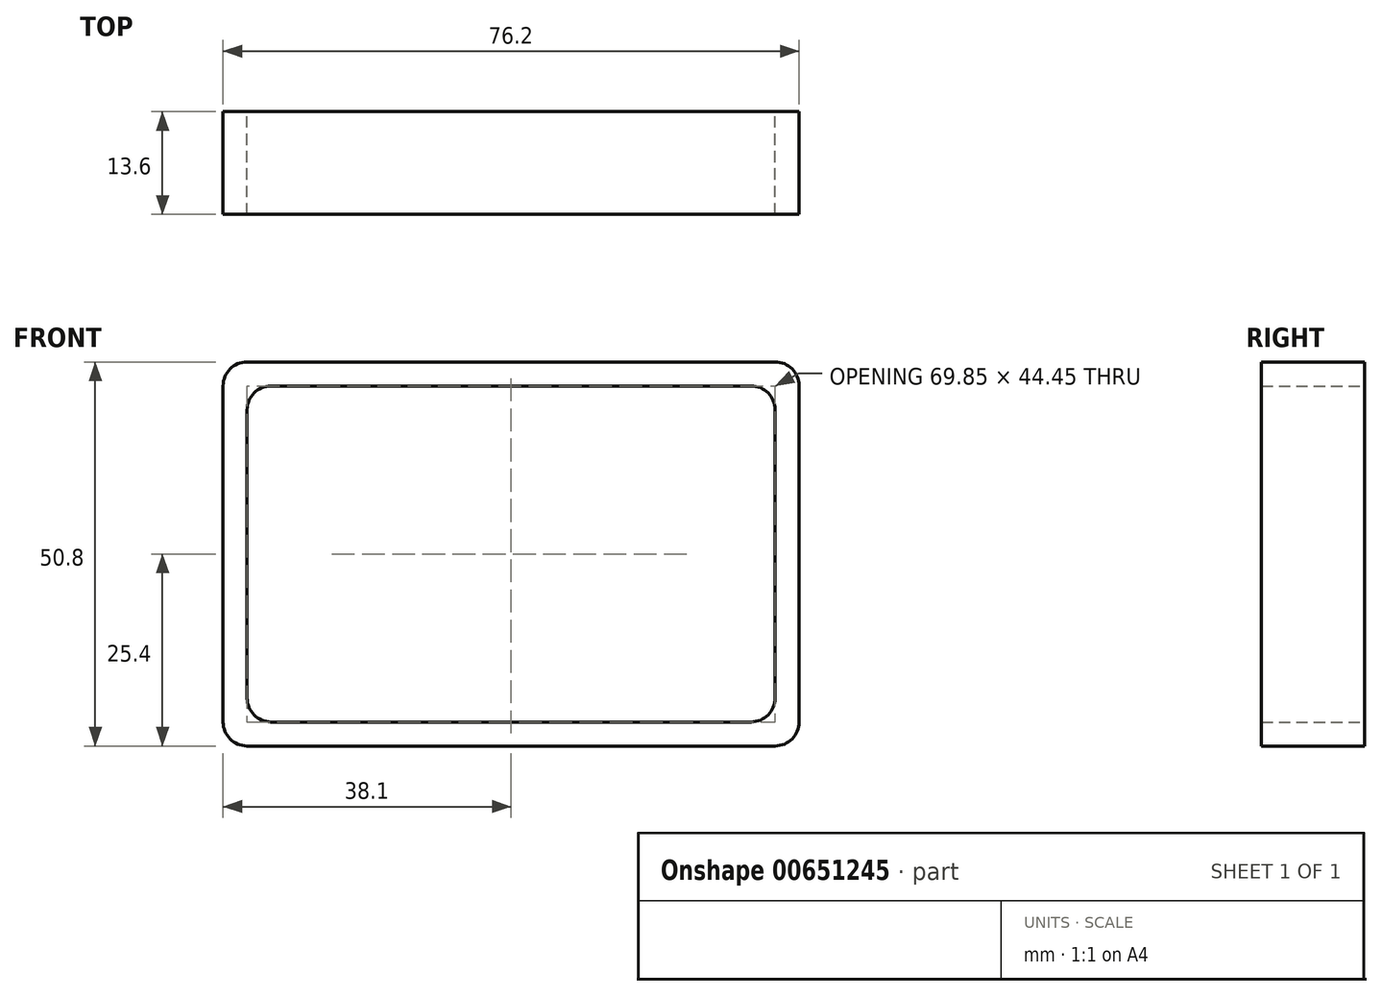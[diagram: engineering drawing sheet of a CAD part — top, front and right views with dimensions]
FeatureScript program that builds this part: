
annotation { "Feature Type Name" : "Feature", "Feature Type Description" : "" }
export const myFeature = defineFeature(function(context is Context, id is Id, definition is map)
    precondition{}
    {
        {
            var Q0;
            Q0=qCreatedBy(makeId("Front.planeOp"),FACE);
            var sketch = newSketch(context, id + "F0", { "sketchPlane" : qUnion([Q0])});
            skLineSegment(sketch, "E0.bottom", {"start": v(38.1, -25.4) * mm, "end": v(-38.1, -25.4) * mm});
            skLineSegment(sketch, "E0.top", {"start": v(38.1, 25.4) * mm, "end": v(-38.1, 25.4) * mm});
            skLineSegment(sketch, "E0.left", {"start": v(38.1, -25.4) * mm, "end": v(38.1, 25.4) * mm});
            skLineSegment(sketch, "E0.right", {"start": v(-38.1, -25.4) * mm, "end": v(-38.1, 25.4) * mm});
            skPoint(sketch, "E0.middle", {"position": v(0, 0) * mm});
            skLineSegment(sketch, "E1.bottom", {"start": v(34.93, -22.22) * mm, "end": v(-34.93, -22.23) * mm});
            skLineSegment(sketch, "E1.top", {"start": v(34.93, 22.23) * mm, "end": v(-34.93, 22.22) * mm});
            skLineSegment(sketch, "E1.left", {"start": v(34.93, -22.22) * mm, "end": v(34.93, 22.23) * mm});
            skLineSegment(sketch, "E1.right", {"start": v(-34.93, -22.23) * mm, "end": v(-34.93, 22.22) * mm});
            skSolve(sketch);
        }
        {
            assignVariable(context, id + "F1", {"name" : "Length", "anyValue" : 13.6});
        }
        {
            var Q0;
            Q0=makeQuery(id+"F0.imprint","IMPRINT",FACE,{"disambiguationData":[TD([[makeQuery(id+"F0.imprint","IMPRINT",EDGE,{"derivedFrom":sQuery(id+"F0.wireOp",EDGE,"E0.bottom")}),-1.0]])]});
            extrude(context, id + "F2", {"entities" : qUnion([Q0]), "depth" : (getVariable(context, 'Length')) * mm, "offsetDistance" : 25.4 * mm});
        }
        {
            var Q0;
            Q0=makeQuery(id+"F2.opExtrude","SWEPT_FACE",FACE,{"disambiguationData":[OSD([sQuery(id+"F0.wireOp",EDGE,"E0.bottom")])]});
            var sketch = newSketch(context, id + "F3", { "sketchPlane" : qUnion([Q0])});
            skLineSegment(sketch, "E2", {"start": v(-38.1, 345.44) * mm, "end": v(38.1, 269.24) * mm});
            skLineSegment(sketch, "E3", {"start": v(38.1, 269.24) * mm, "end": v(38.1, 345.44) * mm});
            skLineSegment(sketch, "E4", {"start": v(38.1, 345.44) * mm, "end": v(-38.1, 345.44) * mm});
            skSolve(sketch);
        }
        {
            var Q0;
            Q0=makeQuery(id+"F3.imprint","IMPRINT",FACE,{"disambiguationData":[TD([[makeQuery(id+"F3.imprint","IMPRINT",EDGE,{"derivedFrom":sQuery(id+"F3.wireOp",EDGE,"E2")}),1.0]])]});
            extrude(context, id + "F4", {"entities" : qUnion([Q0]), "operationType" : NewBodyOperationType.REMOVE, "endBound" : BoundingType.THROUGH_ALL, "oppositeDirection" : true, "depth" : 25.4 * mm, "offsetDistance" : 25.4 * mm});
        }
        {
            var Q0;
            Q0=makeQuery(id+"F2.opExtrude","SWEPT_FACE",FACE,{"disambiguationData":[OSD([sQuery(id+"F0.wireOp",EDGE,"E0.bottom")])]});
            var sketch = newSketch(context, id + "F5", { "sketchPlane" : qUnion([Q0])});
            skLineSegment(sketch, "E5", {"start": v(-38.1, 0) * mm, "end": v(38.1, 76.2) * mm});
            skLineSegment(sketch, "E6", {"start": v(38.1, 76.2) * mm, "end": v(38.1, 0) * mm});
            skLineSegment(sketch, "E7", {"start": v(38.1, 0) * mm, "end": v(-38.1, 0) * mm});
            skSolve(sketch);
        }
        {
            var Q0;
            Q0=makeQuery(id+"F5.imprint","IMPRINT",FACE,{"disambiguationData":[TD([[makeQuery(id+"F5.imprint","IMPRINT",EDGE,{"derivedFrom":sQuery(id+"F5.wireOp",EDGE,"E5")}),-1.0]])]});
            extrude(context, id + "F6", {"entities" : qUnion([Q0]), "operationType" : NewBodyOperationType.REMOVE, "endBound" : BoundingType.THROUGH_ALL, "oppositeDirection" : true, "depth" : 25.4 * mm, "offsetDistance" : 25.4 * mm});
        }
        {
            var Q0;
            Q0=makeQuery(id+"F2.opExtrude","SWEPT_EDGE",EDGE,{"disambiguationData":[OSD([sQuery(id+"F0.wireOp",EDGE,"E0.bottom"),sQuery(id+"F0.wireOp",EDGE,"E0.left")])]});
            var Q1;
            Q1=makeQuery(id+"F2.opExtrude","SWEPT_EDGE",EDGE,{"disambiguationData":[OSD([sQuery(id+"F0.wireOp",EDGE,"E0.bottom"),sQuery(id+"F0.wireOp",EDGE,"E0.right")])]});
            var Q2;
            Q2=makeQuery(id+"F2.opExtrude","SWEPT_EDGE",EDGE,{"disambiguationData":[OSD([sQuery(id+"F0.wireOp",EDGE,"E0.top"),sQuery(id+"F0.wireOp",EDGE,"E0.right")])]});
            var Q3;
            Q3=makeQuery(id+"F2.opExtrude","SWEPT_EDGE",EDGE,{"disambiguationData":[OSD([sQuery(id+"F0.wireOp",EDGE,"E0.top"),sQuery(id+"F0.wireOp",EDGE,"E0.left")])]});
            var Q4;
            Q4=makeQuery(id+"F2.opExtrude","SWEPT_EDGE",EDGE,{"disambiguationData":[OSD([sQuery(id+"F0.wireOp",EDGE,"E1.top"),sQuery(id+"F0.wireOp",EDGE,"E1.right")])]});
            var Q5;
            Q5=makeQuery(id+"F2.opExtrude","SWEPT_EDGE",EDGE,{"disambiguationData":[OSD([sQuery(id+"F0.wireOp",EDGE,"E1.top"),sQuery(id+"F0.wireOp",EDGE,"E1.left")])]});
            var Q6;
            Q6=makeQuery(id+"F2.opExtrude","SWEPT_EDGE",EDGE,{"disambiguationData":[OSD([sQuery(id+"F0.wireOp",EDGE,"E1.bottom"),sQuery(id+"F0.wireOp",EDGE,"E1.right")])]});
            var Q7;
            Q7=makeQuery(id+"F2.opExtrude","SWEPT_EDGE",EDGE,{"disambiguationData":[OSD([sQuery(id+"F0.wireOp",EDGE,"E1.bottom"),sQuery(id+"F0.wireOp",EDGE,"E1.left")])]});
            fillet(context, id + "F7", {"entities" : qUnion([Q0, Q1, Q2, Q3, Q4, Q5, Q6, Q7]), "radius" : 3.17 * mm, "tangentPropagation" : true, "allowEdgeOverflow" : false});
        }
    });
